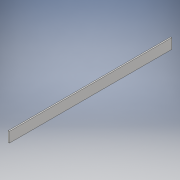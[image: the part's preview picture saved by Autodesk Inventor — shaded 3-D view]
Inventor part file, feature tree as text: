
AUTODESK INVENTOR PART (.ipt)
format: ipt  version: 2017 (Build 210142000, 142)  size: 91,648 bytes
history: native  units: in
note: dims shown in document units (in); Inventor stores cm internally (conversion verified against a paired STEP export)
features: extrude x1, sketch x1
ambient origin geometry x8: Origin, YZ Plane, XZ Plane, XY Plane, X Axis, Y Axis, Z Axis, Center Point
bodies: Solid1 (feature_tree)
feature tree (2):
  extrude  "Extrusion1"  Depth=1.0in
  sketch  "Sketch1"  dims[d0=0.125in d1=1.0in d2=16.0in d3=0.0in]
